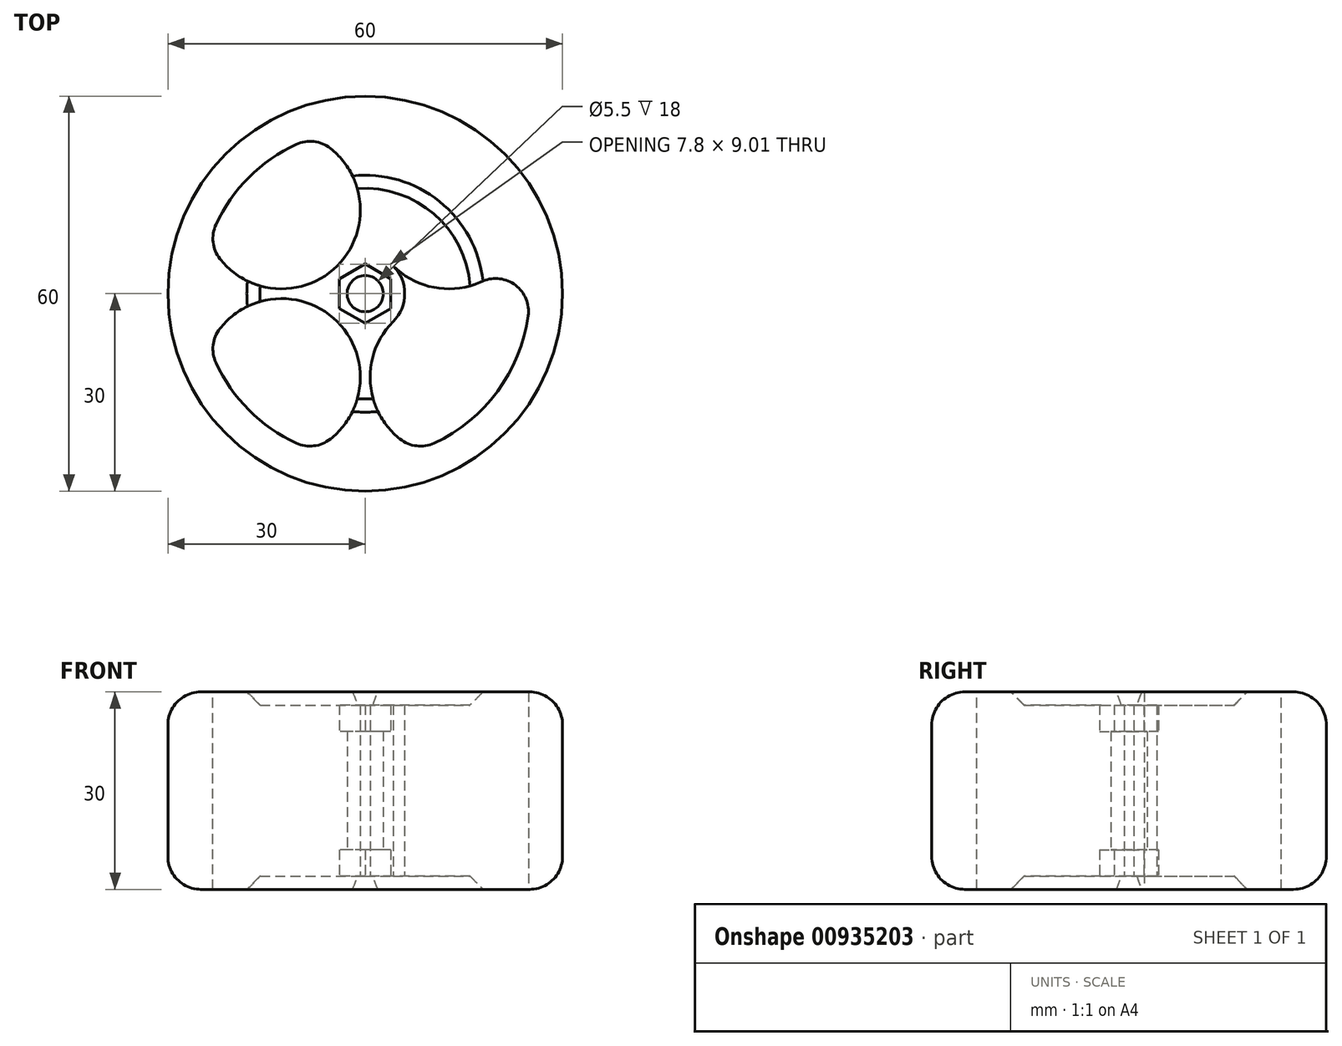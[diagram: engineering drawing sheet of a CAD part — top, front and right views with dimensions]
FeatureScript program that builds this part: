
annotation { "Feature Type Name" : "Feature", "Feature Type Description" : "" }
export const myFeature = defineFeature(function(context is Context, id is Id, definition is map)
    precondition{}
    {
        {
            var Q0;
            Q0=qCreatedBy(makeId("Top.planeOp"),FACE);
            var sketch = newSketch(context, id + "F0", { "sketchPlane" : qUnion([Q0])});
            skCircle(sketch, "E0", {"center": v(0, 0) * mm, "radius": 30 * mm});
            skCircle(sketch, "E1", {"center": v(0, 0) * mm, "radius": 25 * mm});
            skCircle(sketch, "E2", {"center": v(0, 0) * mm, "radius": 6 * mm});
            skArc(sketch, "E3", {"start": v(-23.69, 8) * mm, "mid": v(-4.24, 4.24) * mm, "end": v(-8, 23.69) * mm});
            skArc(sketch, "E4.MirrorCS", {"start": v(23.69, 8) * mm, "mid": v(4.24, 4.24) * mm, "end": v(8, 23.69) * mm});
            skArc(sketch, "E5.MirrorCS", {"start": v(23.69, -8) * mm, "mid": v(4.24, -4.24) * mm, "end": v(8, -23.69) * mm});
            skArc(sketch, "E6.MirrorCS", {"start": v(-23.69, -8) * mm, "mid": v(-4.24, -4.24) * mm, "end": v(-8, -23.69) * mm});
            skCircle(sketch, "E7.cCircle", {"center": v(0, 0) * mm, "radius": 3.9 * mm, "construction": true});
            skLineSegment(sketch, "E7.0", {"start": v(-3.9, -2.25) * mm, "end": v(-3.9, 2.25) * mm});
            skLineSegment(sketch, "E7.1", {"start": v(-3.9, 2.25) * mm, "end": v(0, 4.5) * mm});
            skLineSegment(sketch, "E7.2", {"start": v(0, 4.5) * mm, "end": v(3.9, 2.25) * mm});
            skLineSegment(sketch, "E7.3", {"start": v(3.9, 2.25) * mm, "end": v(3.9, -2.25) * mm});
            skLineSegment(sketch, "E7.4", {"start": v(3.9, -2.25) * mm, "end": v(0, -4.5) * mm});
            skLineSegment(sketch, "E7.5", {"start": v(0, -4.5) * mm, "end": v(-3.9, -2.25) * mm});
            skPoint(sketch, "E7.0.midPoint", {"position": v(-3.9, 0) * mm});
            skCircle(sketch, "E8", {"center": v(0, 0) * mm, "radius": 2.75 * mm});
            skCircle(sketch, "E9", {"center": v(0, 0) * mm, "radius": 3 * mm});
            skSolve(sketch);
        }
        {
            var Q0;
            {var subQ0=sQuery(id+"F0.wireOp",EDGE,"E3");var subQ1=sQuery(id+"F0.wireOp",EDGE,"E1");var subQ2=makeQuery(id+"F0.imprint","INTERSECT",VERTEX,{"disambiguationData":[OD(0.0)],"derivedFrom":[subQ1,subQ0]});Q0=makeQuery(id+"F0.imprint","IMPRINT",FACE,{"disambiguationData":[TD([[makeQuery(id+"F0.imprint","IMPRINT",EDGE,{"disambiguationData":[TD([[subQ2,-1.0]])],"derivedFrom":subQ1}),1.0]])]});}
            var Q1;
            Q1=makeQuery(id+"F0.imprint","IMPRINT",FACE,{"disambiguationData":[TD([[makeQuery(id+"F0.imprint","IMPRINT",EDGE,{"derivedFrom":sQuery(id+"F0.wireOp",EDGE,"E7.0")}),1.0]])]});
            var Q2;
            {var subQ0=sQuery(id+"F0.wireOp",EDGE,"E3");var subQ1=sQuery(id+"F0.wireOp",EDGE,"E1");var subQ2=makeQuery(id+"F0.imprint","INTERSECT",VERTEX,{"disambiguationData":[OD(1.0)],"derivedFrom":[subQ1,subQ0]});Q2=makeQuery(id+"F0.imprint","IMPRINT",FACE,{"disambiguationData":[TD([[makeQuery(id+"F0.imprint","IMPRINT",EDGE,{"disambiguationData":[TD([[subQ2,1.0]])],"derivedFrom":subQ1}),1.0]])]});}
            var Q3;
            {var subQ0=sQuery(id+"F0.wireOp",EDGE,"E4.MirrorCS");var subQ1=sQuery(id+"F0.wireOp",EDGE,"E1");var subQ2=makeQuery(id+"F0.imprint","INTERSECT",VERTEX,{"disambiguationData":[OD(0.0)],"derivedFrom":[subQ1,subQ0]});Q3=makeQuery(id+"F0.imprint","IMPRINT",FACE,{"disambiguationData":[TD([[makeQuery(id+"F0.imprint","IMPRINT",EDGE,{"disambiguationData":[TD([[subQ2,1.0]])],"derivedFrom":subQ1}),1.0]])]});}
            var Q4;
            {var subQ0=sQuery(id+"F0.wireOp",EDGE,"E5.MirrorCS");var subQ1=sQuery(id+"F0.wireOp",EDGE,"E1");var subQ2=makeQuery(id+"F0.imprint","INTERSECT",VERTEX,{"disambiguationData":[OD(1.0)],"derivedFrom":[subQ1,subQ0]});Q4=makeQuery(id+"F0.imprint","IMPRINT",FACE,{"disambiguationData":[TD([[makeQuery(id+"F0.imprint","IMPRINT",EDGE,{"disambiguationData":[TD([[subQ2,1.0]])],"derivedFrom":subQ1}),1.0]])]});}
            var Q5;
            Q5=makeQuery(id+"F0.imprint","IMPRINT",FACE,{"disambiguationData":[TD([[makeQuery(id+"F0.imprint","IMPRINT",EDGE,{"derivedFrom":sQuery(id+"F0.wireOp",EDGE,"o0ada7Xc-SexE-nNEt-rR8g-kgeZITjBpnOf")}),1.0]])]});
            var Q6;
            Q6=makeQuery(id+"F0.imprint","IMPRINT",FACE,{"disambiguationData":[TD([[makeQuery(id+"F0.imprint","IMPRINT",EDGE,{"derivedFrom":sQuery(id+"F0.wireOp",EDGE,"o0ada7Xc-SexE-nNEt-rR8g-kgeZITjBpnOf")}),-1.0]])]});
            var Q7;
            Q7=makeQuery(id+"F0.imprint","IMPRINT",FACE,{"disambiguationData":[TD([[makeQuery(id+"F0.imprint","IMPRINT",EDGE,{"derivedFrom":sQuery(id+"F0.wireOp",EDGE,"E7.0")}),-1.0]])]});
            var Q8;
            Q8=makeQuery(id+"F0.imprint","IMPRINT",FACE,{"disambiguationData":[TD([[makeQuery(id+"F0.imprint","IMPRINT",EDGE,{"derivedFrom":sQuery(id+"F0.wireOp",EDGE,"E0")}),1.0]])]});
            extrude(context, id + "F1", {"entities" : qUnion([Q0, Q1, Q2, Q3, Q4, Q5, Q6, Q7, Q8]), "depth" : 30 * mm, "offsetDistance" : 25 * mm});
        }
        {
            var Q0;
            Q0=makeQuery(id+"F0.imprint","IMPRINT",FACE,{"disambiguationData":[TD([[makeQuery(id+"F0.imprint","IMPRINT",EDGE,{"derivedFrom":sQuery(id+"F0.wireOp",EDGE,"E8")}),-1.0]])]});
            extrude(context, id + "F2", {"entities" : qUnion([Q0]), "operationType" : NewBodyOperationType.ADD, "depth" : 28 * mm, "offsetDistance" : 25 * mm, "hasSecondDirection" : true, "secondDirectionOppositeDirection" : false, "secondDirectionDepth" : 2 * mm});
        }
        {
            var Q0;
            Q0=makeQuery(id+"F1.opExtrude","CAP_EDGE",EDGE,{"disambiguationData":[OSD([sQuery(id+"F0.wireOp",EDGE,"E9")])],"isStart":false});
            var Q1;
            Q1=makeQuery(id+"F1.opExtrude","CAP_EDGE",EDGE,{"disambiguationData":[OSD([sQuery(id+"F0.wireOp",EDGE,"E9")])],"isStart":true});
            chamfer(context, id + "F3", {"entities" : qUnion([Q0, Q1]), "width" : 15 * mm, "tangentPropagation" : true});
        }
        {
            var Q0;
            {var subQ0=sQuery(id+"F0.wireOp",EDGE,"E3");var subQ1=sQuery(id+"F0.wireOp",EDGE,"E1");Q0=makeQuery(id+"F1.opExtrude","SWEPT_EDGE",EDGE,{"disambiguationData":[OSD([subQ1,subQ0]),TDD([makeQuery(id+"F0.imprint","INTERSECT",VERTEX,{"disambiguationData":[OD(1.0)],"derivedFrom":[subQ1,subQ0]})])]});}
            var Q1;
            {var subQ0=sQuery(id+"F0.wireOp",EDGE,"E4.MirrorCS");var subQ1=sQuery(id+"F0.wireOp",EDGE,"E1");Q1=makeQuery(id+"F1.opExtrude","SWEPT_EDGE",EDGE,{"disambiguationData":[OSD([subQ1,subQ0]),TDD([makeQuery(id+"F0.imprint","INTERSECT",VERTEX,{"disambiguationData":[OD(1.0)],"derivedFrom":[subQ1,subQ0]})])]});}
            var Q2;
            {var subQ0=sQuery(id+"F0.wireOp",EDGE,"E4.MirrorCS");var subQ1=sQuery(id+"F0.wireOp",EDGE,"E1");Q2=makeQuery(id+"F1.opExtrude","SWEPT_EDGE",EDGE,{"disambiguationData":[OSD([subQ1,subQ0]),TDD([makeQuery(id+"F0.imprint","INTERSECT",VERTEX,{"disambiguationData":[OD(0.0)],"derivedFrom":[subQ1,subQ0]})])]});}
            var Q3;
            {var subQ0=sQuery(id+"F0.wireOp",EDGE,"E5.MirrorCS");var subQ1=sQuery(id+"F0.wireOp",EDGE,"E1");Q3=makeQuery(id+"F1.opExtrude","SWEPT_EDGE",EDGE,{"disambiguationData":[OSD([subQ1,subQ0]),TDD([makeQuery(id+"F0.imprint","INTERSECT",VERTEX,{"disambiguationData":[OD(0.0)],"derivedFrom":[subQ1,subQ0]})])]});}
            var Q4;
            {var subQ0=sQuery(id+"F0.wireOp",EDGE,"E5.MirrorCS");var subQ1=sQuery(id+"F0.wireOp",EDGE,"E1");Q4=makeQuery(id+"F1.opExtrude","SWEPT_EDGE",EDGE,{"disambiguationData":[OSD([subQ1,subQ0]),TDD([makeQuery(id+"F0.imprint","INTERSECT",VERTEX,{"disambiguationData":[OD(1.0)],"derivedFrom":[subQ1,subQ0]})])]});}
            var Q5;
            {var subQ0=sQuery(id+"F0.wireOp",EDGE,"E3");var subQ1=sQuery(id+"F0.wireOp",EDGE,"E1");Q5=makeQuery(id+"F1.opExtrude","SWEPT_EDGE",EDGE,{"disambiguationData":[OSD([subQ1,subQ0]),TDD([makeQuery(id+"F0.imprint","INTERSECT",VERTEX,{"disambiguationData":[OD(0.0)],"derivedFrom":[subQ1,subQ0]})])]});}
            var Q6;
            {var subQ0=sQuery(id+"F0.wireOp",EDGE,"E6.MirrorCS");var subQ1=sQuery(id+"F0.wireOp",EDGE,"E1");Q6=makeQuery(id+"F1.opExtrude","SWEPT_EDGE",EDGE,{"disambiguationData":[OSD([subQ1,subQ0]),TDD([makeQuery(id+"F0.imprint","INTERSECT",VERTEX,{"disambiguationData":[OD(0.0)],"derivedFrom":[subQ1,subQ0]})])]});}
            var Q7;
            {var subQ0=sQuery(id+"F0.wireOp",EDGE,"E6.MirrorCS");var subQ1=sQuery(id+"F0.wireOp",EDGE,"E1");Q7=makeQuery(id+"F1.opExtrude","SWEPT_EDGE",EDGE,{"disambiguationData":[OSD([subQ1,subQ0]),TDD([makeQuery(id+"F0.imprint","INTERSECT",VERTEX,{"disambiguationData":[OD(1.0)],"derivedFrom":[subQ1,subQ0]})])]});}
            fillet(context, id + "F4", {"entities" : qUnion([Q0, Q1, Q2, Q3, Q4, Q5, Q6, Q7]), "radius" : 5 * mm, "tangentPropagation" : true, "allowEdgeOverflow" : false});
        }
        {
            var Q0;
            Q0=makeQuery(id+"F0.imprint","IMPRINT",FACE,{"disambiguationData":[TD([[makeQuery(id+"F0.imprint","IMPRINT",EDGE,{"derivedFrom":sQuery(id+"F0.wireOp",EDGE,"E7.0")}),-1.0]])]});
            var Q1;
            Q1=makeQuery(id+"F0.imprint","IMPRINT",FACE,{"disambiguationData":[TD([[makeQuery(id+"F0.imprint","IMPRINT",EDGE,{"derivedFrom":sQuery(id+"F0.wireOp",EDGE,"E8")}),-1.0]])]});
            extrude(context, id + "F5", {"entities" : qUnion([Q0, Q1]), "operationType" : NewBodyOperationType.REMOVE, "depth" : 6 * mm, "offsetDistance" : 25 * mm});
        }
        {
            var Q0;
            Q0=makeQuery(id+"F0.imprint","IMPRINT",FACE,{"disambiguationData":[TD([[makeQuery(id+"F0.imprint","IMPRINT",EDGE,{"derivedFrom":sQuery(id+"F0.wireOp",EDGE,"E8")}),-1.0]])]});
            var Q1;
            Q1=makeQuery(id+"F0.imprint","IMPRINT",FACE,{"disambiguationData":[TD([[makeQuery(id+"F0.imprint","IMPRINT",EDGE,{"derivedFrom":sQuery(id+"F0.wireOp",EDGE,"E7.0")}),-1.0]])]});
            var Q2;
            Q2=makeQuery(id+"F2.opExtrude","CAP_FACE",FACE,{"disambiguationData":[OSD([sQuery(id+"F0.wireOp",EDGE,"E8"),sQuery(id+"F0.wireOp",EDGE,"E9")])],"isStart":false});
            extrude(context, id + "F6", {"entities" : qUnion([Q0, Q1]), "operationType" : NewBodyOperationType.REMOVE, "endBound" : BoundingType.UP_TO_SURFACE, "depth" : 25 * mm, "endBoundEntityFace" : qUnion([Q2]), "offsetDistance" : 25 * mm, "hasSecondDirection" : true, "secondDirectionOppositeDirection" : false, "secondDirectionDepth" : 24 * mm});
        }
        {
            var Q0;
            Q0=makeQuery(id+"F1.opExtrude","CAP_EDGE",EDGE,{"disambiguationData":[OSD([sQuery(id+"F0.wireOp",EDGE,"E0")])],"isStart":false});
            var Q1;
            Q1=makeQuery(id+"F1.opExtrude","CAP_EDGE",EDGE,{"disambiguationData":[OSD([sQuery(id+"F0.wireOp",EDGE,"E0")])],"isStart":true});
            fillet(context, id + "F7", {"entities" : qUnion([Q0, Q1]), "radius" : 5 * mm, "tangentPropagation" : true, "allowEdgeOverflow" : false});
        }
    });
